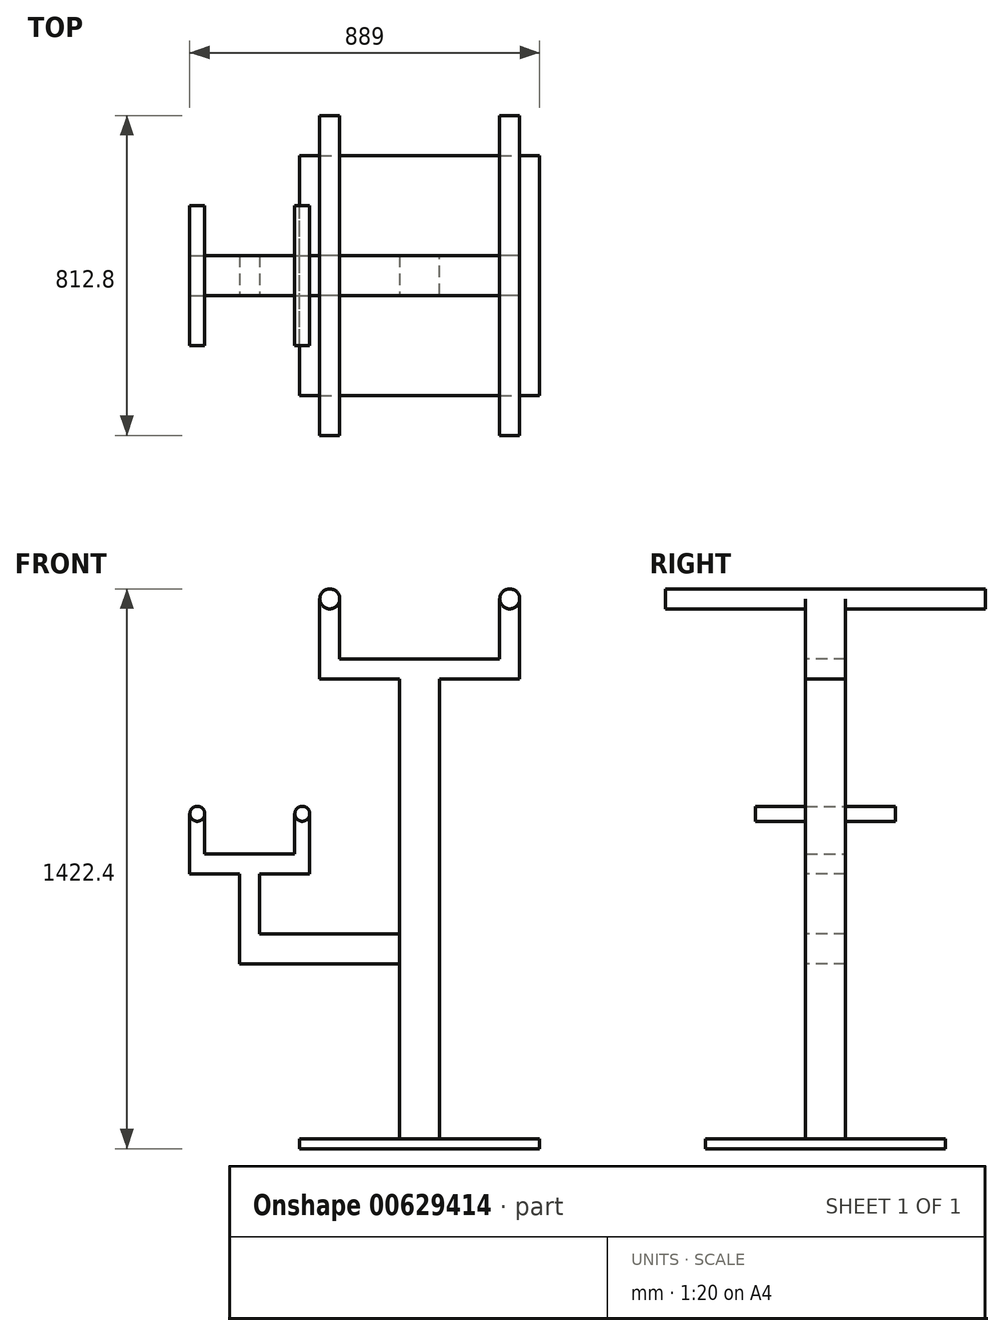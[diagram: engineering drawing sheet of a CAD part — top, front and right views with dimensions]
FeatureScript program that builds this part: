
annotation { "Feature Type Name" : "Feature", "Feature Type Description" : "" }
export const myFeature = defineFeature(function(context is Context, id is Id, definition is map)
    precondition{}
    {
        {
            var Q0;
            Q0=qCreatedBy(makeId("Top.planeOp"),FACE);
            var sketch = newSketch(context, id + "F0", { "sketchPlane" : qUnion([Q0])});
            skLineSegment(sketch, "E0.bottom", {"start": v(0, 0) * mm, "end": v(609.6, 0) * mm});
            skLineSegment(sketch, "E0.top", {"start": v(0, 609.6) * mm, "end": v(609.6, 609.6) * mm});
            skLineSegment(sketch, "E0.left", {"start": v(0, 0) * mm, "end": v(0, 609.6) * mm});
            skLineSegment(sketch, "E0.right", {"start": v(609.6, 0) * mm, "end": v(609.6, 609.6) * mm});
            skSolve(sketch);
        }
        {
            var Q0;
            Q0 = qSketchRegion(id + "F0", true);
            extrude(context, id + "F1", {"entities" : qUnion([Q0]), "depth" : 25.4 * mm, "offsetDistance" : 25.4 * mm});
        }
        {
            var Q0;
            Q0=makeQuery(id+"F1.opExtrude","CAP_FACE",FACE,{"disambiguationData":[OSD([sQuery(id+"F0.wireOp",EDGE,"E0.bottom"),sQuery(id+"F0.wireOp",EDGE,"E0.top"),sQuery(id+"F0.wireOp",EDGE,"E0.left"),sQuery(id+"F0.wireOp",EDGE,"E0.right")])],"isStart":false});
            var sketch = newSketch(context, id + "F2", { "sketchPlane" : qUnion([Q0])});
            skPoint(sketch, "E1.firstSnap0", {"position": v(304.8, 0) * mm});
            skLineSegment(sketch, "E1.bottom", {"start": v(254, 254) * mm, "end": v(355.6, 254) * mm});
            skLineSegment(sketch, "E1.top", {"start": v(254, 355.6) * mm, "end": v(355.6, 355.6) * mm});
            skLineSegment(sketch, "E1.left", {"start": v(254, 254) * mm, "end": v(254, 355.6) * mm});
            skLineSegment(sketch, "E1.right", {"start": v(355.6, 254) * mm, "end": v(355.6, 355.6) * mm});
            skSolve(sketch);
        }
        {
            var Q0;
            Q0 = qSketchRegion(id + "F2", true);
            extrude(context, id + "F3", {"entities" : qUnion([Q0]), "operationType" : NewBodyOperationType.ADD, "depth" : 1168.4 * mm, "offsetDistance" : 25.4 * mm});
        }
        {
            var Q0;
            Q0=makeQuery(id+"F3.opExtrude","CAP_FACE",FACE,{"disambiguationData":[OSD([sQuery(id+"F2.wireOp",EDGE,"E1.bottom"),sQuery(id+"F2.wireOp",EDGE,"E1.top"),sQuery(id+"F2.wireOp",EDGE,"E1.left"),sQuery(id+"F2.wireOp",EDGE,"E1.right")])],"isStart":false});
            var sketch = newSketch(context, id + "F4", { "sketchPlane" : qUnion([Q0])});
            skLineSegment(sketch, "E2.bottom", {"start": v(50.8, 355.6) * mm, "end": v(558.8, 355.6) * mm});
            skLineSegment(sketch, "E2.top", {"start": v(50.8, 254) * mm, "end": v(558.8, 254) * mm});
            skLineSegment(sketch, "E2.left", {"start": v(50.8, 355.6) * mm, "end": v(50.8, 254) * mm});
            skLineSegment(sketch, "E2.right", {"start": v(558.8, 355.6) * mm, "end": v(558.8, 254) * mm});
            skSolve(sketch);
        }
        {
            var Q0;
            Q0 = qSketchRegion(id + "F4", true);
            extrude(context, id + "F5", {"entities" : qUnion([Q0]), "operationType" : NewBodyOperationType.ADD, "depth" : 50.8 * mm, "offsetDistance" : 25.4 * mm});
        }
        {
            var Q0;
            Q0=makeQuery(id+"F5.opExtrude","CAP_FACE",FACE,{"disambiguationData":[OSD([sQuery(id+"F4.wireOp",EDGE,"E2.bottom"),sQuery(id+"F4.wireOp",EDGE,"E2.top"),sQuery(id+"F4.wireOp",EDGE,"E2.left"),sQuery(id+"F4.wireOp",EDGE,"E2.right")])],"isStart":false});
            var sketch = newSketch(context, id + "F6", { "sketchPlane" : qUnion([Q0])});
            skLineSegment(sketch, "E3.bottom", {"start": v(50.8, 355.6) * mm, "end": v(101.6, 355.6) * mm});
            skLineSegment(sketch, "E3.top", {"start": v(50.8, 254) * mm, "end": v(101.6, 254) * mm});
            skLineSegment(sketch, "E3.left", {"start": v(50.8, 355.6) * mm, "end": v(50.8, 254) * mm});
            skLineSegment(sketch, "E3.right", {"start": v(101.6, 355.6) * mm, "end": v(101.6, 254) * mm});
            skLineSegment(sketch, "E4.bottom", {"start": v(558.8, 355.6) * mm, "end": v(508, 355.6) * mm});
            skLineSegment(sketch, "E4.top", {"start": v(558.8, 254) * mm, "end": v(508, 254) * mm});
            skLineSegment(sketch, "E4.left", {"start": v(558.8, 355.6) * mm, "end": v(558.8, 254) * mm});
            skLineSegment(sketch, "E4.right", {"start": v(508, 355.6) * mm, "end": v(508, 254) * mm});
            skSolve(sketch);
        }
        {
            var Q0;
            Q0 = qSketchRegion(id + "F6", true);
            extrude(context, id + "F7", {"entities" : qUnion([Q0]), "operationType" : NewBodyOperationType.ADD, "depth" : 152.4 * mm, "offsetDistance" : 25.4 * mm});
        }
        {
            var Q0;
            Q0=makeQuery(id+"F7.boolean.opBoolean","MERGE",FACE,{"derivedFrom":[makeQuery(id+"F5.boolean.opBoolean","MERGE",FACE,{"derivedFrom":[makeQuery(id+"F3.opExtrude","SWEPT_FACE",FACE,{"disambiguationData":[OSD([sQuery(id+"F2.wireOp",EDGE,"E1.bottom")])]}),makeQuery(id+"F5.opExtrude","SWEPT_FACE",FACE,{"disambiguationData":[OSD([sQuery(id+"F4.wireOp",EDGE,"E2.top")])]})]}),makeQuery(id+"F7.opExtrude","SWEPT_FACE",FACE,{"disambiguationData":[OSD([sQuery(id+"F6.wireOp",EDGE,"E3.top")])]}),makeQuery(id+"F7.opExtrude","SWEPT_FACE",FACE,{"disambiguationData":[OSD([sQuery(id+"F6.wireOp",EDGE,"E4.top")])]})]});
            var sketch = newSketch(context, id + "F8", { "sketchPlane" : qUnion([Q0])});
            skCircle(sketch, "E5", {"center": v(76.2, 1397) * mm, "radius": 25.4 * mm});
            skCircle(sketch, "E6", {"center": v(533.4, 1397) * mm, "radius": 25.4 * mm});
            skSolve(sketch);
        }
        {
            var Q0;
            Q0 = qSketchRegion(id + "F8", true);
            extrude(context, id + "F9", {"entities" : qUnion([Q0]), "operationType" : NewBodyOperationType.ADD, "depth" : 355.6 * mm, "offsetDistance" : 25.4 * mm, "hasSecondDirection" : true, "secondDirectionOppositeDirection" : true, "secondDirectionDepth" : 457.2 * mm});
        }
        {
            var Q0;
            Q0=makeQuery(id+"F3.opExtrude","SWEPT_FACE",FACE,{"disambiguationData":[OSD([sQuery(id+"F2.wireOp",EDGE,"E1.left")])]});
            var sketch = newSketch(context, id + "F10", { "sketchPlane" : qUnion([Q0])});
            skLineSegment(sketch, "E7.bottom", {"start": v(485.74, 808.53) * mm, "end": v(587.34, 808.53) * mm});
            skLineSegment(sketch, "E7.top", {"start": v(485.74, 732.33) * mm, "end": v(587.34, 732.33) * mm});
            skLineSegment(sketch, "E7.left", {"start": v(485.74, 808.53) * mm, "end": v(485.74, 732.33) * mm});
            skLineSegment(sketch, "E7.right", {"start": v(587.34, 808.53) * mm, "end": v(587.34, 732.33) * mm});
            skSolve(sketch);
        }
        {
            var Q0;
            Q0 = qSketchRegion(id + "F10", true);
            extrude(context, id + "F11", {"entities" : qUnion([Q0]), "depth" : 406.4 * mm, "offsetDistance" : 25.4 * mm});
        }
        {
            var Q0;
            Q0=makeQuery(id+"F11.opExtrude","SWEPT_FACE",FACE,{"disambiguationData":[OSD([sQuery(id+"F10.wireOp",EDGE,"E7.bottom")])]});
            var sketch = newSketch(context, id + "F12", { "sketchPlane" : qUnion([Q0])});
            skLineSegment(sketch, "E8.bottom", {"start": v(-152.4, -485.74) * mm, "end": v(-101.6, -485.74) * mm});
            skLineSegment(sketch, "E8.top", {"start": v(-152.4, -587.34) * mm, "end": v(-101.6, -587.34) * mm});
            skLineSegment(sketch, "E8.left", {"start": v(-152.4, -485.74) * mm, "end": v(-152.4, -587.34) * mm});
            skLineSegment(sketch, "E8.right", {"start": v(-101.6, -485.74) * mm, "end": v(-101.6, -587.34) * mm});
            skSolve(sketch);
        }
        {
            var Q0;
            Q0 = qSketchRegion(id + "F12", true);
            extrude(context, id + "F13", {"entities" : qUnion([Q0]), "operationType" : NewBodyOperationType.ADD, "depth" : 152.4 * mm, "offsetDistance" : 25.4 * mm});
        }
        {
            var Q0;
            Q0=makeQuery(id+"F13.opExtrude","CAP_FACE",FACE,{"disambiguationData":[OSD([sQuery(id+"F12.wireOp",EDGE,"E8.bottom"),sQuery(id+"F12.wireOp",EDGE,"E8.top"),sQuery(id+"F12.wireOp",EDGE,"E8.left"),sQuery(id+"F12.wireOp",EDGE,"E8.right")])],"isStart":false});
            var sketch = newSketch(context, id + "F14", { "sketchPlane" : qUnion([Q0])});
            skLineSegment(sketch, "E9.bottom", {"start": v(-279.4, -485.74) * mm, "end": v(25.4, -485.74) * mm});
            skLineSegment(sketch, "E9.top", {"start": v(-279.4, -587.34) * mm, "end": v(25.4, -587.34) * mm});
            skLineSegment(sketch, "E9.left", {"start": v(-279.4, -485.74) * mm, "end": v(-279.4, -587.34) * mm});
            skLineSegment(sketch, "E9.right", {"start": v(25.4, -485.74) * mm, "end": v(25.4, -587.34) * mm});
            skSolve(sketch);
        }
        {
            var Q0;
            Q0 = qSketchRegion(id + "F14", true);
            extrude(context, id + "F15", {"entities" : qUnion([Q0]), "operationType" : NewBodyOperationType.ADD, "depth" : 50.8 * mm, "offsetDistance" : 25.4 * mm});
        }
        {
            var Q0;
            Q0=makeQuery(id+"F15.opExtrude","CAP_FACE",FACE,{"disambiguationData":[OSD([sQuery(id+"F14.wireOp",EDGE,"E9.bottom"),sQuery(id+"F14.wireOp",EDGE,"E9.top"),sQuery(id+"F14.wireOp",EDGE,"E9.left"),sQuery(id+"F14.wireOp",EDGE,"E9.right")])],"isStart":false});
            var sketch = newSketch(context, id + "F16", { "sketchPlane" : qUnion([Q0])});
            skLineSegment(sketch, "E10.bottom", {"start": v(-279.4, -485.74) * mm, "end": v(-241.3, -485.74) * mm});
            skLineSegment(sketch, "E10.top", {"start": v(-279.4, -587.34) * mm, "end": v(-241.3, -587.34) * mm});
            skLineSegment(sketch, "E10.left", {"start": v(-279.4, -485.74) * mm, "end": v(-279.4, -587.34) * mm});
            skLineSegment(sketch, "E10.right", {"start": v(-241.3, -485.74) * mm, "end": v(-241.3, -587.34) * mm});
            skLineSegment(sketch, "E11.bottom", {"start": v(25.4, -587.34) * mm, "end": v(-12.7, -587.34) * mm});
            skLineSegment(sketch, "E11.top", {"start": v(25.4, -485.74) * mm, "end": v(-12.7, -485.74) * mm});
            skLineSegment(sketch, "E11.left", {"start": v(25.4, -587.34) * mm, "end": v(25.4, -485.74) * mm});
            skLineSegment(sketch, "E11.right", {"start": v(-12.7, -587.34) * mm, "end": v(-12.7, -485.74) * mm});
            skSolve(sketch);
        }
        {
            var Q0;
            Q0 = qSketchRegion(id + "F16", true);
            extrude(context, id + "F17", {"entities" : qUnion([Q0]), "operationType" : NewBodyOperationType.ADD, "depth" : 101.6 * mm, "offsetDistance" : 25.4 * mm});
        }
        {
            var Q0;
            Q0=makeQuery(id+"F17.boolean.opBoolean","MERGE",FACE,{"derivedFrom":[makeQuery(id+"F15.boolean.opBoolean","MERGE",FACE,{"derivedFrom":[makeQuery(id+"F13.boolean.opBoolean","MERGE",FACE,{"derivedFrom":[makeQuery(id+"F11.opExtrude","SWEPT_FACE",FACE,{"disambiguationData":[OSD([sQuery(id+"F10.wireOp",EDGE,"E7.right")])]}),makeQuery(id+"F13.opExtrude","SWEPT_FACE",FACE,{"disambiguationData":[OSD([sQuery(id+"F12.wireOp",EDGE,"E8.top")])]})]}),makeQuery(id+"F15.opExtrude","SWEPT_FACE",FACE,{"disambiguationData":[OSD([sQuery(id+"F14.wireOp",EDGE,"E9.top")])]})]}),makeQuery(id+"F17.opExtrude","SWEPT_FACE",FACE,{"disambiguationData":[OSD([sQuery(id+"F16.wireOp",EDGE,"E10.top")])]}),makeQuery(id+"F17.opExtrude","SWEPT_FACE",FACE,{"disambiguationData":[OSD([sQuery(id+"F16.wireOp",EDGE,"E11.bottom")])]})]});
            var sketch = newSketch(context, id + "F18", { "sketchPlane" : qUnion([Q0])});
            skCircle(sketch, "E12", {"center": v(-260.35, 1113.33) * mm, "radius": 19.05 * mm});
            skCircle(sketch, "E13", {"center": v(6.35, 1113.33) * mm, "radius": 19.05 * mm});
            skSolve(sketch);
        }
        {
            var Q0;
            Q0 = qSketchRegion(id + "F18", true);
            extrude(context, id + "F19", {"entities" : qUnion([Q0]), "operationType" : NewBodyOperationType.ADD, "depth" : 127 * mm, "offsetDistance" : 25.4 * mm, "hasSecondDirection" : true, "secondDirectionOppositeDirection" : true, "secondDirectionDepth" : 228.6 * mm});
        }
        {
            var Q0;
            Q0=makeQuery(id+"F11.opExtrude","CAP_EDGE",EDGE,{"disambiguationData":[OSD([sQuery(id+"F10.wireOp",EDGE,"E7.right")])],"isStart":true});
            cPoint(context, id + "F20", {"entities" : qUnion([Q0]), "parameter" : 0.5});
        }
        {
            var Q0;
            Q0=makeQuery(id+"F3.opExtrude","SWEPT_EDGE",EDGE,{"disambiguationData":[OSD([sQuery(id+"F2.wireOp",EDGE,"E1.bottom"),sQuery(id+"F2.wireOp",EDGE,"E1.left")])]});
            cPoint(context, id + "F21", {"entities" : qUnion([Q0]), "parameter" : 0.5});
        }
        {
            var Q0;
            Q0=makeQuery(id+"F11.opExtrude","SWEPT_BODY",BODY,{"disambiguationData":[OSD([sQuery(id+"F10.wireOp",EDGE,"E7.bottom"),sQuery(id+"F10.wireOp",EDGE,"E7.top"),sQuery(id+"F10.wireOp",EDGE,"E7.left"),sQuery(id+"F10.wireOp",EDGE,"E7.right")])]});
            var Q1;
            Q1 = qCreatedBy(id + "F20" ,VERTEX);
            var Q2;
            Q2 = qCreatedBy(id + "F21" ,VERTEX);
            transform(context, id + "F22", {"entities" : qUnion([Q0]), "transformType" : TransformType.TRANSLATION_ENTITY, "oppositeDirectionEntity" : false, "transformLine" : qUnion([Q1, Q2]), "makeCopy" : false});
        }
        {
            var Q0;
            Q0=makeQuery(id+"F11.opExtrude","SWEPT_BODY",BODY,{"disambiguationData":[OSD([sQuery(id+"F10.wireOp",EDGE,"E7.bottom"),sQuery(id+"F10.wireOp",EDGE,"E7.top"),sQuery(id+"F10.wireOp",EDGE,"E7.left"),sQuery(id+"F10.wireOp",EDGE,"E7.right")])]});
            var Q1;
            Q1=makeQuery(id+"F3.opExtrude","SWEPT_EDGE",EDGE,{"disambiguationData":[OSD([sQuery(id+"F2.wireOp",EDGE,"E1.bottom"),sQuery(id+"F2.wireOp",EDGE,"E1.left")])]});
            transform(context, id + "F23", {"entities" : qUnion([Q0]), "transformType" : TransformType.TRANSLATION_DISTANCE, "transformDirection" : qUnion([Q1]), "distance" : 101.6 * mm, "makeCopy" : false});
        }
    });
